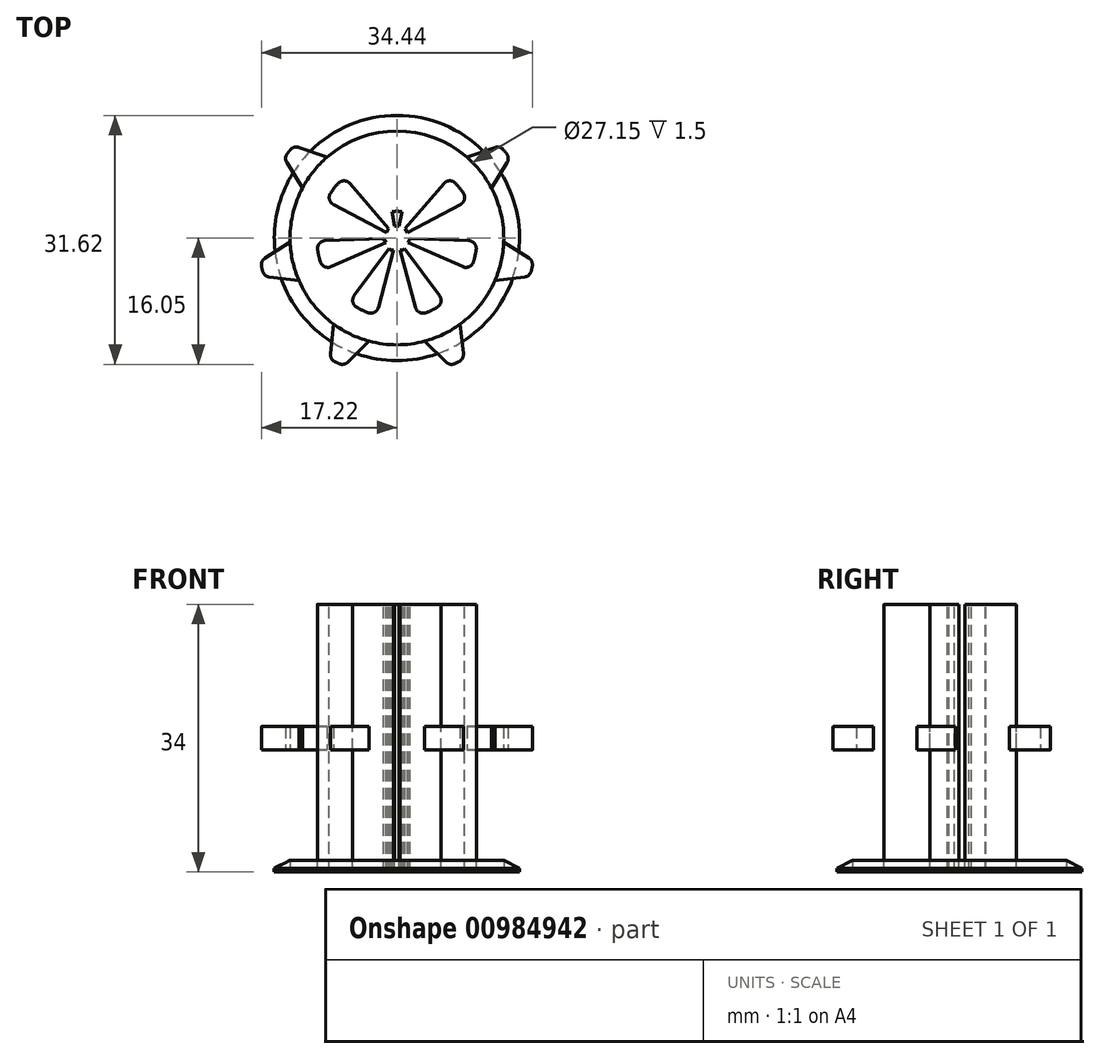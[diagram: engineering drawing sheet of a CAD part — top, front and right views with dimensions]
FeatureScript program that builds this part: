
annotation { "Feature Type Name" : "Feature", "Feature Type Description" : "" }
export const myFeature = defineFeature(function(context is Context, id is Id, definition is map)
    precondition{}
    {
        {
            var Q0;
            Q0=qCreatedBy(makeId("Top.planeOp"),FACE);
            var sketch = newSketch(context, id + "F0", { "sketchPlane" : qUnion([Q0])});
            skCircle(sketch, "E0", {"center": v(0, 0) * mm, "radius": 13.57 * mm});
            skSolve(sketch);
        }
        {
            var Q0;
            Q0=makeQuery(id+"F0.imprint","IMPRINT",FACE,{"disambiguationData":[TD([[makeQuery(id+"F0.imprint","IMPRINT",EDGE,{"derivedFrom":sQuery(id+"F0.wireOp",EDGE,"E0")}),1.0]])]});
            extrude(context, id + "F1", {"entities" : qUnion([Q0]), "endBound" : BoundingType.SYMMETRIC, "depth" : 34 * mm, "offsetDistance" : 25 * mm});
        }
        {
            var Q0;
            Q0=qCreatedBy(makeId("Top.planeOp"),FACE);
            var sketch = newSketch(context, id + "F2", { "sketchPlane" : qUnion([Q0])});
            skPoint(sketch, "E1", {"position": v(0, 17.57) * mm});
            skPoint(sketch, "E2", {"position": v(15.3, 12.2) * mm});
            skPoint(sketch, "E3", {"position": v(19.08, -4.36) * mm});
            skPoint(sketch, "E4", {"position": v(8.5, -17.64) * mm});
            skPoint(sketch, "E5", {"position": v(-8.5, -17.64) * mm});
            skPoint(sketch, "E6", {"position": v(-19.08, -4.36) * mm});
            skPoint(sketch, "E7", {"position": v(-15.3, 12.2) * mm});
            skArc(sketch, "E8", {"start": v(-1, 17.55) * mm, "mid": v(0, 17.57) * mm, "end": v(1, 17.55) * mm});
            skPoint(sketch, "E9", {"position": v(-12.18, 9.71) * mm});
            skPoint(sketch, "E10", {"position": v(12.18, 9.71) * mm});
            skPoint(sketch, "E11", {"position": v(15.18, -3.47) * mm});
            skPoint(sketch, "E12", {"position": v(6.76, -14.03) * mm});
            skPoint(sketch, "E13", {"position": v(-6.76, -14.03) * mm});
            skPoint(sketch, "E14", {"position": v(-15.18, -3.47) * mm});
            skPoint(sketch, "E15", {"position": v(0, 13.57) * mm});
            skArc(sketch, "E16", {"start": v(-2.5, 13.34) * mm, "mid": v(0, 13.57) * mm, "end": v(2.5, 13.34) * mm});
            skLineSegment(sketch, "E17", {"start": v(-2.5, 13.34) * mm, "end": v(-1, 17.55) * mm});
            skLineSegment(sketch, "E18", {"start": v(1, 17.55) * mm, "end": v(2.5, 13.34) * mm});
            skLineSegment(sketch, "E19.1.0", {"start": v(14.34, 10.16) * mm, "end": v(11.99, 6.36) * mm});
            skArc(sketch, "E19.1.1", {"start": v(8.87, 10.27) * mm, "mid": v(10.61, 8.46) * mm, "end": v(11.99, 6.36) * mm});
            skLineSegment(sketch, "E19.1.2", {"start": v(8.87, 10.27) * mm, "end": v(13.1, 11.72) * mm});
            skArc(sketch, "E19.1.3", {"start": v(13.1, 11.72) * mm, "mid": v(13.74, 10.96) * mm, "end": v(14.34, 10.16) * mm});
            skLineSegment(sketch, "E19.2.0", {"start": v(16.88, -4.88) * mm, "end": v(12.45, -5.4) * mm});
            skArc(sketch, "E19.2.1", {"start": v(13.56, -0.53) * mm, "mid": v(13.23, -3.02) * mm, "end": v(12.45, -5.4) * mm});
            skLineSegment(sketch, "E19.2.2", {"start": v(13.56, -0.53) * mm, "end": v(17.33, -2.93) * mm});
            skArc(sketch, "E19.2.3", {"start": v(17.33, -2.93) * mm, "mid": v(17.13, -3.91) * mm, "end": v(16.88, -4.88) * mm});
            skLineSegment(sketch, "E19.3.0", {"start": v(6.71, -16.24) * mm, "end": v(3.54, -13.1) * mm});
            skArc(sketch, "E19.3.1", {"start": v(8.04, -10.94) * mm, "mid": v(5.89, -12.23) * mm, "end": v(3.54, -13.1) * mm});
            skLineSegment(sketch, "E19.3.2", {"start": v(8.04, -10.94) * mm, "end": v(8.51, -15.37) * mm});
            skArc(sketch, "E19.3.3", {"start": v(8.51, -15.37) * mm, "mid": v(7.63, -15.83) * mm, "end": v(6.71, -16.24) * mm});
            skLineSegment(sketch, "E19.4.0", {"start": v(-8.51, -15.37) * mm, "end": v(-8.04, -10.94) * mm});
            skArc(sketch, "E19.4.1", {"start": v(-3.54, -13.1) * mm, "mid": v(-5.89, -12.23) * mm, "end": v(-8.04, -10.94) * mm});
            skLineSegment(sketch, "E19.4.2", {"start": v(-3.54, -13.1) * mm, "end": v(-6.71, -16.24) * mm});
            skArc(sketch, "E19.4.3", {"start": v(-6.71, -16.24) * mm, "mid": v(-7.63, -15.83) * mm, "end": v(-8.51, -15.37) * mm});
            skLineSegment(sketch, "E19.5.0", {"start": v(-17.33, -2.93) * mm, "end": v(-13.56, -0.53) * mm});
            skArc(sketch, "E19.5.1", {"start": v(-12.45, -5.4) * mm, "mid": v(-13.23, -3.02) * mm, "end": v(-13.56, -0.53) * mm});
            skLineSegment(sketch, "E19.5.2", {"start": v(-12.45, -5.4) * mm, "end": v(-16.88, -4.88) * mm});
            skArc(sketch, "E19.5.3", {"start": v(-16.88, -4.88) * mm, "mid": v(-17.13, -3.91) * mm, "end": v(-17.33, -2.93) * mm});
            skLineSegment(sketch, "E19.6.0", {"start": v(-13.1, 11.72) * mm, "end": v(-8.87, 10.27) * mm});
            skArc(sketch, "E19.6.1", {"start": v(-11.99, 6.36) * mm, "mid": v(-10.61, 8.46) * mm, "end": v(-8.87, 10.27) * mm});
            skLineSegment(sketch, "E19.6.2", {"start": v(-11.99, 6.36) * mm, "end": v(-14.34, 10.16) * mm});
            skArc(sketch, "E19.6.3", {"start": v(-14.34, 10.16) * mm, "mid": v(-13.74, 10.96) * mm, "end": v(-13.1, 11.72) * mm});
            skLineSegment(sketch, "E19.anchor1", {"start": v(0, 0) * mm, "end": v(2.5, 13.34) * mm, "construction": true});
            skLineSegment(sketch, "E19.anchor2", {"start": v(0, 0) * mm, "end": v(-8.87, 10.27) * mm, "construction": true});
            skSolve(sketch);
        }
        {
            var Q0;
            Q0=makeQuery(id+"F2.imprint","IMPRINT",FACE,{"disambiguationData":[TD([[makeQuery(id+"F2.imprint","IMPRINT",EDGE,{"derivedFrom":sQuery(id+"F2.wireOp",EDGE,"E19.6.0")}),-1.0]])]});
            var Q1;
            Q1=makeQuery(id+"F2.imprint","IMPRINT",FACE,{"disambiguationData":[TD([[makeQuery(id+"F2.imprint","IMPRINT",EDGE,{"derivedFrom":sQuery(id+"F2.wireOp",EDGE,"E8")}),-1.0]])]});
            var Q2;
            Q2=makeQuery(id+"F2.imprint","IMPRINT",FACE,{"disambiguationData":[TD([[makeQuery(id+"F2.imprint","IMPRINT",EDGE,{"derivedFrom":sQuery(id+"F2.wireOp",EDGE,"E19.1.0")}),-1.0]])]});
            var Q3;
            Q3=makeQuery(id+"F2.imprint","IMPRINT",FACE,{"disambiguationData":[TD([[makeQuery(id+"F2.imprint","IMPRINT",EDGE,{"derivedFrom":sQuery(id+"F2.wireOp",EDGE,"E19.2.0")}),-1.0]])]});
            var Q4;
            Q4=makeQuery(id+"F2.imprint","IMPRINT",FACE,{"disambiguationData":[TD([[makeQuery(id+"F2.imprint","IMPRINT",EDGE,{"derivedFrom":sQuery(id+"F2.wireOp",EDGE,"E19.3.0")}),-1.0]])]});
            var Q5;
            Q5=makeQuery(id+"F2.imprint","IMPRINT",FACE,{"disambiguationData":[TD([[makeQuery(id+"F2.imprint","IMPRINT",EDGE,{"derivedFrom":sQuery(id+"F2.wireOp",EDGE,"E19.4.0")}),-1.0]])]});
            var Q6;
            Q6=makeQuery(id+"F2.imprint","IMPRINT",FACE,{"disambiguationData":[TD([[makeQuery(id+"F2.imprint","IMPRINT",EDGE,{"derivedFrom":sQuery(id+"F2.wireOp",EDGE,"E19.5.0")}),-1.0]])]});
            extrude(context, id + "F3", {"entities" : qUnion([Q0, Q1, Q2, Q3, Q4, Q5, Q6]), "operationType" : NewBodyOperationType.ADD, "endBound" : BoundingType.SYMMETRIC, "depth" : 3 * mm, "offsetDistance" : 25 * mm});
        }
        {
            var Q0;
            Q0=makeQuery(id+"F1.opExtrude","CAP_FACE",FACE,{"disambiguationData":[OSD([sQuery(id+"F0.wireOp",EDGE,"E0")])],"isStart":false});
            var sketch = newSketch(context, id + "F4", { "sketchPlane" : qUnion([Q0])});
            skLineSegment(sketch, "E20", {"start": v(0, 0) * mm, "end": v(0, 3.4) * mm});
            skLineSegment(sketch, "E21", {"start": v(0, 3.4) * mm, "end": v(0, 6.79) * mm});
            skLineSegment(sketch, "E22", {"start": v(0, 6.79) * mm, "end": v(0, 10.18) * mm});
            skLineSegment(sketch, "E23", {"start": v(0, 10.18) * mm, "end": v(0, 13.57) * mm});
            skArc(sketch, "E24", {"start": v(-1.9, 10) * mm, "mid": v(0, 10.18) * mm, "end": v(1.9, 10) * mm});
            skPoint(sketch, "E25", {"position": v(0, 10.18) * mm});
            skArc(sketch, "E26", {"start": v(-0.63, 3.33) * mm, "mid": v(0, 3.4) * mm, "end": v(0.63, 3.33) * mm});
            skPoint(sketch, "E27", {"position": v(0, 3.4) * mm});
            skLineSegment(sketch, "E28", {"start": v(0, 0) * mm, "end": v(-1.9, 10) * mm});
            skLineSegment(sketch, "E29", {"start": v(1.9, 10) * mm, "end": v(0, 0) * mm});
            skArc(sketch, "E30.1.0", {"start": v(-9, 4.75) * mm, "mid": v(-7.96, 6.35) * mm, "end": v(-6.64, 7.72) * mm});
            skLineSegment(sketch, "E30.1.1", {"start": v(-6.64, 7.72) * mm, "end": v(0, 0) * mm});
            skArc(sketch, "E30.1.2", {"start": v(-3, 1.58) * mm, "mid": v(-2.65, 2.12) * mm, "end": v(-2.21, 2.57) * mm});
            skLineSegment(sketch, "E30.1.3", {"start": v(0, 0) * mm, "end": v(-9, 4.75) * mm});
            skArc(sketch, "E30.2.0", {"start": v(-9.33, -4.07) * mm, "mid": v(-9.93, -2.27) * mm, "end": v(-10.17, -0.38) * mm});
            skLineSegment(sketch, "E30.2.1", {"start": v(-10.17, -0.38) * mm, "end": v(0, 0) * mm});
            skArc(sketch, "E30.2.2", {"start": v(-3.1, -1.36) * mm, "mid": v(-3.3, -0.76) * mm, "end": v(-3.4, -0.13) * mm});
            skLineSegment(sketch, "E30.2.3", {"start": v(0, 0) * mm, "end": v(-9.33, -4.07) * mm});
            skArc(sketch, "E30.3.0", {"start": v(-2.63, -9.83) * mm, "mid": v(-4.42, -9.17) * mm, "end": v(-6.05, -8.19) * mm});
            skLineSegment(sketch, "E30.3.1", {"start": v(-6.05, -8.19) * mm, "end": v(0, 0) * mm});
            skArc(sketch, "E30.3.2", {"start": v(-0.88, -3.28) * mm, "mid": v(-1.47, -3.06) * mm, "end": v(-2.02, -2.73) * mm});
            skLineSegment(sketch, "E30.3.3", {"start": v(0, 0) * mm, "end": v(-2.63, -9.83) * mm});
            skArc(sketch, "E30.4.0", {"start": v(6.05, -8.19) * mm, "mid": v(4.42, -9.17) * mm, "end": v(2.63, -9.83) * mm});
            skLineSegment(sketch, "E30.4.1", {"start": v(2.63, -9.83) * mm, "end": v(0, 0) * mm});
            skArc(sketch, "E30.4.2", {"start": v(2.02, -2.73) * mm, "mid": v(1.47, -3.06) * mm, "end": v(0.88, -3.28) * mm});
            skLineSegment(sketch, "E30.4.3", {"start": v(0, 0) * mm, "end": v(6.05, -8.19) * mm});
            skArc(sketch, "E30.5.0", {"start": v(10.17, -0.38) * mm, "mid": v(9.93, -2.27) * mm, "end": v(9.33, -4.07) * mm});
            skLineSegment(sketch, "E30.5.1", {"start": v(9.33, -4.07) * mm, "end": v(0, 0) * mm});
            skArc(sketch, "E30.5.2", {"start": v(3.4, -0.13) * mm, "mid": v(3.3, -0.76) * mm, "end": v(3.1, -1.36) * mm});
            skLineSegment(sketch, "E30.5.3", {"start": v(0, 0) * mm, "end": v(10.17, -0.38) * mm});
            skArc(sketch, "E30.6.0", {"start": v(6.64, 7.72) * mm, "mid": v(7.96, 6.35) * mm, "end": v(9, 4.75) * mm});
            skLineSegment(sketch, "E30.6.1", {"start": v(9, 4.75) * mm, "end": v(0, 0) * mm});
            skArc(sketch, "E30.6.2", {"start": v(2.21, 2.57) * mm, "mid": v(2.65, 2.12) * mm, "end": v(3, 1.58) * mm});
            skLineSegment(sketch, "E30.6.3", {"start": v(0, 0) * mm, "end": v(6.64, 7.72) * mm});
            skCircle(sketch, "E31.cCircle", {"center": v(0, 0) * mm, "radius": 1.5 * mm, "construction": true});
            skLineSegment(sketch, "E31.0", {"start": v(-0.87, 1.5) * mm, "end": v(0.87, 1.5) * mm});
            skLineSegment(sketch, "E31.1", {"start": v(0.87, 1.5) * mm, "end": v(1.73, 0) * mm});
            skLineSegment(sketch, "E31.2", {"start": v(1.73, 0) * mm, "end": v(0.87, -1.5) * mm});
            skLineSegment(sketch, "E31.3", {"start": v(0.87, -1.5) * mm, "end": v(-0.87, -1.5) * mm});
            skLineSegment(sketch, "E31.4", {"start": v(-0.87, -1.5) * mm, "end": v(-1.73, 0) * mm});
            skLineSegment(sketch, "E31.5", {"start": v(-1.73, 0) * mm, "end": v(-0.87, 1.5) * mm});
            skPoint(sketch, "E31.0.midPoint", {"position": v(0, 1.5) * mm});
            skSolve(sketch);
        }
        {
            var Q0;
            {var subQ0=sQuery(id+"F4.wireOp",EDGE,"E30.1.0");Q0=makeQuery(id+"F4.imprint","IMPRINT",FACE,{"disambiguationData":[TD([[makeQuery(id+"F4.imprint","IMPRINT",EDGE,{"derivedFrom":subQ0}),-1.0]])]});}
            var Q1;
            {var subQ1=sQuery(id+"F4.wireOp",EDGE,"E21");Q1=makeQuery(id+"F4.imprint","IMPRINT",FACE,{"disambiguationData":[TD([[makeQuery(id+"F4.imprint","IMPRINT",EDGE,{"derivedFrom":subQ1}),1.0]])]});}
            var Q2;
            {var subQ5=sQuery(id+"F4.wireOp",EDGE,"E21");Q2=makeQuery(id+"F4.imprint","IMPRINT",FACE,{"disambiguationData":[TD([[makeQuery(id+"F4.imprint","IMPRINT",EDGE,{"derivedFrom":subQ5}),-1.0]])]});}
            var Q3;
            {var subQ0=sQuery(id+"F4.wireOp",EDGE,"E30.6.0");Q3=makeQuery(id+"F4.imprint","IMPRINT",FACE,{"disambiguationData":[TD([[makeQuery(id+"F4.imprint","IMPRINT",EDGE,{"derivedFrom":subQ0}),-1.0]])]});}
            var Q4;
            {var subQ0=sQuery(id+"F4.wireOp",EDGE,"E30.5.0");Q4=makeQuery(id+"F4.imprint","IMPRINT",FACE,{"disambiguationData":[TD([[makeQuery(id+"F4.imprint","IMPRINT",EDGE,{"derivedFrom":subQ0}),-1.0]])]});}
            var Q5;
            {var subQ0=sQuery(id+"F4.wireOp",EDGE,"E30.4.0");Q5=makeQuery(id+"F4.imprint","IMPRINT",FACE,{"disambiguationData":[TD([[makeQuery(id+"F4.imprint","IMPRINT",EDGE,{"derivedFrom":subQ0}),-1.0]])]});}
            var Q6;
            {var subQ0=sQuery(id+"F4.wireOp",EDGE,"E30.3.0");Q6=makeQuery(id+"F4.imprint","IMPRINT",FACE,{"disambiguationData":[TD([[makeQuery(id+"F4.imprint","IMPRINT",EDGE,{"derivedFrom":subQ0}),-1.0]])]});}
            var Q7;
            {var subQ0=sQuery(id+"F4.wireOp",EDGE,"E30.2.0");Q7=makeQuery(id+"F4.imprint","IMPRINT",FACE,{"disambiguationData":[TD([[makeQuery(id+"F4.imprint","IMPRINT",EDGE,{"derivedFrom":subQ0}),-1.0]])]});}
            var Q8;
            {var subQ3=sQuery(id+"F4.wireOp",EDGE,"83845be1-feb7-4ae9-bd42-3e984bab1aa7.5");var subQ5=sQuery(id+"F4.wireOp",EDGE,"83845be1-feb7-4ae9-bd42-3e984bab1aa7.4");var subQ7=makeQuery(id+"F4.imprint","INTERSECT",VERTEX,{"derivedFrom":[subQ5,subQ3]});Q8=makeQuery(id+"F4.imprint","IMPRINT",FACE,{"disambiguationData":[TD([[makeQuery(id+"F4.imprint","IMPRINT",EDGE,{"disambiguationData":[TD([[subQ7,1.0]])],"derivedFrom":subQ5}),-1.0]])]});}
            var Q9;
            {var subQ1=sQuery(id+"F4.wireOp",EDGE,"E28");var subQ3=sQuery(id+"F4.wireOp",EDGE,"83845be1-feb7-4ae9-bd42-3e984bab1aa7.5");var subQ4=makeQuery(id+"F4.imprint","INTERSECT",VERTEX,{"derivedFrom":[subQ1,subQ3]});Q9=makeQuery(id+"F4.imprint","IMPRINT",FACE,{"disambiguationData":[TD([[makeQuery(id+"F4.imprint","IMPRINT",EDGE,{"disambiguationData":[TD([[subQ4,1.0]])],"derivedFrom":subQ3}),-1.0]])]});}
            var Q10;
            {var subQ0=sQuery(id+"F4.wireOp",EDGE,"E28");var subQ3=sQuery(id+"F4.wireOp",EDGE,"83845be1-feb7-4ae9-bd42-3e984bab1aa7.5");var subQ5=makeQuery(id+"F4.imprint","INTERSECT",VERTEX,{"derivedFrom":[subQ0,subQ3]});Q10=makeQuery(id+"F4.imprint","IMPRINT",FACE,{"disambiguationData":[TD([[makeQuery(id+"F4.imprint","IMPRINT",EDGE,{"disambiguationData":[TD([[subQ5,-1.0]])],"derivedFrom":subQ3}),-1.0]])]});}
            var Q11;
            {var subQ0=sQuery(id+"F4.wireOp",EDGE,"E29");var subQ3=sQuery(id+"F4.wireOp",EDGE,"83845be1-feb7-4ae9-bd42-3e984bab1aa7.0");var subQ5=makeQuery(id+"F4.imprint","INTERSECT",VERTEX,{"derivedFrom":[subQ0,subQ3]});Q11=makeQuery(id+"F4.imprint","IMPRINT",FACE,{"disambiguationData":[TD([[makeQuery(id+"F4.imprint","IMPRINT",EDGE,{"disambiguationData":[TD([[subQ5,1.0]])],"derivedFrom":subQ3}),-1.0]])]});}
            var Q12;
            {var subQ1=sQuery(id+"F4.wireOp",EDGE,"E29");var subQ3=sQuery(id+"F4.wireOp",EDGE,"83845be1-feb7-4ae9-bd42-3e984bab1aa7.0");var subQ4=makeQuery(id+"F4.imprint","INTERSECT",VERTEX,{"derivedFrom":[subQ1,subQ3]});Q12=makeQuery(id+"F4.imprint","IMPRINT",FACE,{"disambiguationData":[TD([[makeQuery(id+"F4.imprint","IMPRINT",EDGE,{"disambiguationData":[TD([[subQ4,-1.0]])],"derivedFrom":subQ3}),-1.0]])]});}
            var Q13;
            {var subQ3=sQuery(id+"F4.wireOp",EDGE,"83845be1-feb7-4ae9-bd42-3e984bab1aa7.1");var subQ5=sQuery(id+"F4.wireOp",EDGE,"83845be1-feb7-4ae9-bd42-3e984bab1aa7.0");var subQ7=makeQuery(id+"F4.imprint","INTERSECT",VERTEX,{"derivedFrom":[subQ5,subQ3]});Q13=makeQuery(id+"F4.imprint","IMPRINT",FACE,{"disambiguationData":[TD([[makeQuery(id+"F4.imprint","IMPRINT",EDGE,{"disambiguationData":[TD([[subQ7,1.0]])],"derivedFrom":subQ5}),-1.0]])]});}
            var Q14;
            {var subQ1=sQuery(id+"F4.wireOp",EDGE,"E30.5.3");var subQ3=sQuery(id+"F4.wireOp",EDGE,"83845be1-feb7-4ae9-bd42-3e984bab1aa7.1");var subQ4=makeQuery(id+"F4.imprint","INTERSECT",VERTEX,{"derivedFrom":[subQ1,subQ3]});Q14=makeQuery(id+"F4.imprint","IMPRINT",FACE,{"disambiguationData":[TD([[makeQuery(id+"F4.imprint","IMPRINT",EDGE,{"disambiguationData":[TD([[subQ4,1.0]])],"derivedFrom":subQ3}),-1.0]])]});}
            var Q15;
            {var subQ1=sQuery(id+"F4.wireOp",EDGE,"E30.5.1");var subQ3=sQuery(id+"F4.wireOp",EDGE,"83845be1-feb7-4ae9-bd42-3e984bab1aa7.1");var subQ4=makeQuery(id+"F4.imprint","INTERSECT",VERTEX,{"derivedFrom":[subQ1,subQ3]});Q15=makeQuery(id+"F4.imprint","IMPRINT",FACE,{"disambiguationData":[TD([[makeQuery(id+"F4.imprint","IMPRINT",EDGE,{"disambiguationData":[TD([[subQ4,1.0]])],"derivedFrom":subQ3}),-1.0]])]});}
            var Q16;
            {var subQ3=sQuery(id+"F4.wireOp",EDGE,"83845be1-feb7-4ae9-bd42-3e984bab1aa7.2");var subQ5=sQuery(id+"F4.wireOp",EDGE,"83845be1-feb7-4ae9-bd42-3e984bab1aa7.1");var subQ6=makeQuery(id+"F4.imprint","INTERSECT",VERTEX,{"derivedFrom":[subQ5,subQ3]});Q16=makeQuery(id+"F4.imprint","IMPRINT",FACE,{"disambiguationData":[TD([[makeQuery(id+"F4.imprint","IMPRINT",EDGE,{"disambiguationData":[TD([[subQ6,1.0]])],"derivedFrom":subQ5}),-1.0]])]});}
            var Q17;
            {var subQ1=sQuery(id+"F4.wireOp",EDGE,"E30.4.1");var subQ3=sQuery(id+"F4.wireOp",EDGE,"83845be1-feb7-4ae9-bd42-3e984bab1aa7.2");var subQ4=makeQuery(id+"F4.imprint","INTERSECT",VERTEX,{"derivedFrom":[subQ1,subQ3]});Q17=makeQuery(id+"F4.imprint","IMPRINT",FACE,{"disambiguationData":[TD([[makeQuery(id+"F4.imprint","IMPRINT",EDGE,{"disambiguationData":[TD([[subQ4,1.0]])],"derivedFrom":subQ3}),-1.0]])]});}
            var Q18;
            {var subQ3=sQuery(id+"F4.wireOp",EDGE,"83845be1-feb7-4ae9-bd42-3e984bab1aa7.3");var subQ5=sQuery(id+"F4.wireOp",EDGE,"83845be1-feb7-4ae9-bd42-3e984bab1aa7.2");var subQ7=makeQuery(id+"F4.imprint","INTERSECT",VERTEX,{"derivedFrom":[subQ5,subQ3]});Q18=makeQuery(id+"F4.imprint","IMPRINT",FACE,{"disambiguationData":[TD([[makeQuery(id+"F4.imprint","IMPRINT",EDGE,{"disambiguationData":[TD([[subQ7,1.0]])],"derivedFrom":subQ5}),-1.0]])]});}
            var Q19;
            {var subQ1=sQuery(id+"F4.wireOp",EDGE,"E30.3.1");var subQ3=sQuery(id+"F4.wireOp",EDGE,"83845be1-feb7-4ae9-bd42-3e984bab1aa7.3");var subQ4=makeQuery(id+"F4.imprint","INTERSECT",VERTEX,{"derivedFrom":[subQ1,subQ3]});Q19=makeQuery(id+"F4.imprint","IMPRINT",FACE,{"disambiguationData":[TD([[makeQuery(id+"F4.imprint","IMPRINT",EDGE,{"disambiguationData":[TD([[subQ4,1.0]])],"derivedFrom":subQ3}),-1.0]])]});}
            var Q20;
            {var subQ3=sQuery(id+"F4.wireOp",EDGE,"83845be1-feb7-4ae9-bd42-3e984bab1aa7.4");var subQ5=sQuery(id+"F4.wireOp",EDGE,"83845be1-feb7-4ae9-bd42-3e984bab1aa7.3");var subQ7=makeQuery(id+"F4.imprint","INTERSECT",VERTEX,{"derivedFrom":[subQ5,subQ3]});Q20=makeQuery(id+"F4.imprint","IMPRINT",FACE,{"disambiguationData":[TD([[makeQuery(id+"F4.imprint","IMPRINT",EDGE,{"disambiguationData":[TD([[subQ7,1.0]])],"derivedFrom":subQ5}),-1.0]])]});}
            var Q21;
            {var subQ1=sQuery(id+"F4.wireOp",EDGE,"E30.2.1");var subQ3=sQuery(id+"F4.wireOp",EDGE,"83845be1-feb7-4ae9-bd42-3e984bab1aa7.4");var subQ4=makeQuery(id+"F4.imprint","INTERSECT",VERTEX,{"derivedFrom":[subQ1,subQ3]});Q21=makeQuery(id+"F4.imprint","IMPRINT",FACE,{"disambiguationData":[TD([[makeQuery(id+"F4.imprint","IMPRINT",EDGE,{"disambiguationData":[TD([[subQ4,1.0]])],"derivedFrom":subQ3}),-1.0]])]});}
            var Q22;
            {var subQ1=sQuery(id+"F4.wireOp",EDGE,"E30.1.3");var subQ3=sQuery(id+"F4.wireOp",EDGE,"83845be1-feb7-4ae9-bd42-3e984bab1aa7.4");var subQ4=makeQuery(id+"F4.imprint","INTERSECT",VERTEX,{"derivedFrom":[subQ1,subQ3]});Q22=makeQuery(id+"F4.imprint","IMPRINT",FACE,{"disambiguationData":[TD([[makeQuery(id+"F4.imprint","IMPRINT",EDGE,{"disambiguationData":[TD([[subQ4,1.0]])],"derivedFrom":subQ3}),-1.0]])]});}
            var Q23;
            {var subQ3=sQuery(id+"F4.wireOp",EDGE,"E31.2");var subQ5=sQuery(id+"F4.wireOp",EDGE,"E31.1");var subQ7=makeQuery(id+"F4.imprint","INTERSECT",VERTEX,{"derivedFrom":[subQ5,subQ3]});Q23=makeQuery(id+"F4.imprint","IMPRINT",FACE,{"disambiguationData":[TD([[makeQuery(id+"F4.imprint","IMPRINT",EDGE,{"disambiguationData":[TD([[subQ7,1.0]])],"derivedFrom":subQ5}),-1.0]])]});}
            var Q24;
            {var subQ1=sQuery(id+"F4.wireOp",EDGE,"E30.5.1");var subQ3=sQuery(id+"F4.wireOp",EDGE,"E31.2");var subQ4=makeQuery(id+"F4.imprint","INTERSECT",VERTEX,{"derivedFrom":[subQ1,subQ3]});Q24=makeQuery(id+"F4.imprint","IMPRINT",FACE,{"disambiguationData":[TD([[makeQuery(id+"F4.imprint","IMPRINT",EDGE,{"disambiguationData":[TD([[subQ4,1.0]])],"derivedFrom":subQ3}),-1.0]])]});}
            var Q25;
            {var subQ1=sQuery(id+"F4.wireOp",EDGE,"E30.4.3");var subQ3=sQuery(id+"F4.wireOp",EDGE,"E31.2");var subQ4=makeQuery(id+"F4.imprint","INTERSECT",VERTEX,{"derivedFrom":[subQ1,subQ3]});Q25=makeQuery(id+"F4.imprint","IMPRINT",FACE,{"disambiguationData":[TD([[makeQuery(id+"F4.imprint","IMPRINT",EDGE,{"disambiguationData":[TD([[subQ4,1.0]])],"derivedFrom":subQ3}),-1.0]])]});}
            var Q26;
            {var subQ3=sQuery(id+"F4.wireOp",EDGE,"E31.3");var subQ5=sQuery(id+"F4.wireOp",EDGE,"E31.2");var subQ7=makeQuery(id+"F4.imprint","INTERSECT",VERTEX,{"derivedFrom":[subQ5,subQ3]});Q26=makeQuery(id+"F4.imprint","IMPRINT",FACE,{"disambiguationData":[TD([[makeQuery(id+"F4.imprint","IMPRINT",EDGE,{"disambiguationData":[TD([[subQ7,1.0]])],"derivedFrom":subQ5}),-1.0]])]});}
            var Q27;
            {var subQ1=sQuery(id+"F4.wireOp",EDGE,"E30.3.3");var subQ3=sQuery(id+"F4.wireOp",EDGE,"E31.3");var subQ4=makeQuery(id+"F4.imprint","INTERSECT",VERTEX,{"derivedFrom":[subQ1,subQ3]});Q27=makeQuery(id+"F4.imprint","IMPRINT",FACE,{"disambiguationData":[TD([[makeQuery(id+"F4.imprint","IMPRINT",EDGE,{"disambiguationData":[TD([[subQ4,1.0]])],"derivedFrom":subQ3}),-1.0]])]});}
            var Q28;
            {var subQ3=sQuery(id+"F4.wireOp",EDGE,"E31.4");var subQ5=sQuery(id+"F4.wireOp",EDGE,"E31.3");var subQ7=makeQuery(id+"F4.imprint","INTERSECT",VERTEX,{"derivedFrom":[subQ5,subQ3]});Q28=makeQuery(id+"F4.imprint","IMPRINT",FACE,{"disambiguationData":[TD([[makeQuery(id+"F4.imprint","IMPRINT",EDGE,{"disambiguationData":[TD([[subQ7,1.0]])],"derivedFrom":subQ5}),-1.0]])]});}
            var Q29;
            {var subQ1=sQuery(id+"F4.wireOp",EDGE,"E30.2.3");var subQ3=sQuery(id+"F4.wireOp",EDGE,"E31.4");var subQ4=makeQuery(id+"F4.imprint","INTERSECT",VERTEX,{"derivedFrom":[subQ1,subQ3]});Q29=makeQuery(id+"F4.imprint","IMPRINT",FACE,{"disambiguationData":[TD([[makeQuery(id+"F4.imprint","IMPRINT",EDGE,{"disambiguationData":[TD([[subQ4,1.0]])],"derivedFrom":subQ3}),-1.0]])]});}
            var Q30;
            {var subQ1=sQuery(id+"F4.wireOp",EDGE,"E30.2.1");var subQ3=sQuery(id+"F4.wireOp",EDGE,"E31.4");var subQ4=makeQuery(id+"F4.imprint","INTERSECT",VERTEX,{"derivedFrom":[subQ1,subQ3]});Q30=makeQuery(id+"F4.imprint","IMPRINT",FACE,{"disambiguationData":[TD([[makeQuery(id+"F4.imprint","IMPRINT",EDGE,{"disambiguationData":[TD([[subQ4,1.0]])],"derivedFrom":subQ3}),-1.0]])]});}
            var Q31;
            {var subQ3=sQuery(id+"F4.wireOp",EDGE,"E31.5");var subQ5=sQuery(id+"F4.wireOp",EDGE,"E31.4");var subQ6=makeQuery(id+"F4.imprint","INTERSECT",VERTEX,{"derivedFrom":[subQ5,subQ3]});Q31=makeQuery(id+"F4.imprint","IMPRINT",FACE,{"disambiguationData":[TD([[makeQuery(id+"F4.imprint","IMPRINT",EDGE,{"disambiguationData":[TD([[subQ6,1.0]])],"derivedFrom":subQ5}),-1.0]])]});}
            var Q32;
            {var subQ1=sQuery(id+"F4.wireOp",EDGE,"E30.1.1");var subQ3=sQuery(id+"F4.wireOp",EDGE,"E31.5");var subQ4=makeQuery(id+"F4.imprint","INTERSECT",VERTEX,{"derivedFrom":[subQ1,subQ3]});Q32=makeQuery(id+"F4.imprint","IMPRINT",FACE,{"disambiguationData":[TD([[makeQuery(id+"F4.imprint","IMPRINT",EDGE,{"disambiguationData":[TD([[subQ4,1.0]])],"derivedFrom":subQ3}),-1.0]])]});}
            var Q33;
            {var subQ3=sQuery(id+"F4.wireOp",EDGE,"E31.0");var subQ5=sQuery(id+"F4.wireOp",EDGE,"E31.5");var subQ7=makeQuery(id+"F4.imprint","INTERSECT",VERTEX,{"derivedFrom":[subQ3,subQ5]});Q33=makeQuery(id+"F4.imprint","IMPRINT",FACE,{"disambiguationData":[TD([[makeQuery(id+"F4.imprint","IMPRINT",EDGE,{"disambiguationData":[TD([[subQ7,-1.0]])],"derivedFrom":subQ3}),-1.0]])]});}
            var Q34;
            {var subQ1=sQuery(id+"F4.wireOp",EDGE,"E20");var subQ3=sQuery(id+"F4.wireOp",EDGE,"E31.0");var subQ4=makeQuery(id+"F4.imprint","INTERSECT",VERTEX,{"derivedFrom":[subQ1,subQ3]});Q34=makeQuery(id+"F4.imprint","IMPRINT",FACE,{"disambiguationData":[TD([[makeQuery(id+"F4.imprint","IMPRINT",EDGE,{"disambiguationData":[TD([[subQ4,1.0]])],"derivedFrom":subQ3}),-1.0]])]});}
            var Q35;
            {var subQ1=sQuery(id+"F4.wireOp",EDGE,"E20");var subQ3=sQuery(id+"F4.wireOp",EDGE,"E31.0");var subQ4=makeQuery(id+"F4.imprint","INTERSECT",VERTEX,{"derivedFrom":[subQ1,subQ3]});Q35=makeQuery(id+"F4.imprint","IMPRINT",FACE,{"disambiguationData":[TD([[makeQuery(id+"F4.imprint","IMPRINT",EDGE,{"disambiguationData":[TD([[subQ4,-1.0]])],"derivedFrom":subQ3}),-1.0]])]});}
            var Q36;
            {var subQ3=sQuery(id+"F4.wireOp",EDGE,"E31.0");var subQ5=sQuery(id+"F4.wireOp",EDGE,"E31.1");var subQ7=makeQuery(id+"F4.imprint","INTERSECT",VERTEX,{"derivedFrom":[subQ3,subQ5]});Q36=makeQuery(id+"F4.imprint","IMPRINT",FACE,{"disambiguationData":[TD([[makeQuery(id+"F4.imprint","IMPRINT",EDGE,{"disambiguationData":[TD([[subQ7,1.0]])],"derivedFrom":subQ3}),-1.0]])]});}
            var Q37;
            {var subQ1=sQuery(id+"F4.wireOp",EDGE,"E30.6.1");var subQ3=sQuery(id+"F4.wireOp",EDGE,"E31.1");var subQ4=makeQuery(id+"F4.imprint","INTERSECT",VERTEX,{"derivedFrom":[subQ1,subQ3]});Q37=makeQuery(id+"F4.imprint","IMPRINT",FACE,{"disambiguationData":[TD([[makeQuery(id+"F4.imprint","IMPRINT",EDGE,{"disambiguationData":[TD([[subQ4,1.0]])],"derivedFrom":subQ3}),-1.0]])]});}
            extrude(context, id + "F5", {"entities" : qUnion([Q0, Q1, Q2, Q3, Q4, Q5, Q6, Q7, Q8, Q9, Q10, Q11, Q12, Q13, Q14, Q15, Q16, Q17, Q18, Q19, Q20, Q21, Q22, Q23, Q24, Q25, Q26, Q27, Q28, Q29, Q30, Q31, Q32, Q33, Q34, Q35, Q36, Q37]), "operationType" : NewBodyOperationType.REMOVE, "oppositeDirection" : true, "depth" : 34 * mm, "offsetDistance" : 25 * mm});
        }
        {
            var Q0;
            Q0=makeQuery(id+"F5.boolean.opBoolean","COPY",EDGE,{"derivedFrom":makeQuery(id+"F5.opExtrude","SWEPT_EDGE",EDGE,{"disambiguationData":[OSD([sQuery(id+"F4.wireOp",EDGE,"E30.3.0"),sQuery(id+"F4.wireOp",EDGE,"E30.3.1")])]})});
            var Q1;
            Q1=makeQuery(id+"F5.boolean.opBoolean","COPY",EDGE,{"derivedFrom":makeQuery(id+"F5.opExtrude","SWEPT_EDGE",EDGE,{"disambiguationData":[OSD([sQuery(id+"F4.wireOp",EDGE,"E30.3.0"),sQuery(id+"F4.wireOp",EDGE,"E30.3.3")])]})});
            var Q2;
            Q2=makeQuery(id+"F5.boolean.opBoolean","COPY",EDGE,{"derivedFrom":makeQuery(id+"F5.opExtrude","SWEPT_EDGE",EDGE,{"disambiguationData":[OSD([sQuery(id+"F4.wireOp",EDGE,"E30.4.0"),sQuery(id+"F4.wireOp",EDGE,"E30.4.1")])]})});
            var Q3;
            Q3=makeQuery(id+"F5.boolean.opBoolean","COPY",EDGE,{"derivedFrom":makeQuery(id+"F5.opExtrude","SWEPT_EDGE",EDGE,{"disambiguationData":[OSD([sQuery(id+"F4.wireOp",EDGE,"E30.4.0"),sQuery(id+"F4.wireOp",EDGE,"E30.4.3")])]})});
            var Q4;
            Q4=makeQuery(id+"F5.boolean.opBoolean","COPY",EDGE,{"derivedFrom":makeQuery(id+"F5.opExtrude","SWEPT_EDGE",EDGE,{"disambiguationData":[OSD([sQuery(id+"F4.wireOp",EDGE,"E30.5.0"),sQuery(id+"F4.wireOp",EDGE,"E30.5.1")])]})});
            var Q5;
            Q5=makeQuery(id+"F5.boolean.opBoolean","COPY",EDGE,{"derivedFrom":makeQuery(id+"F5.opExtrude","SWEPT_EDGE",EDGE,{"disambiguationData":[OSD([sQuery(id+"F4.wireOp",EDGE,"E30.2.0"),sQuery(id+"F4.wireOp",EDGE,"E30.2.3")])]})});
            var Q6;
            Q6=makeQuery(id+"F5.boolean.opBoolean","COPY",EDGE,{"derivedFrom":makeQuery(id+"F5.opExtrude","SWEPT_EDGE",EDGE,{"disambiguationData":[OSD([sQuery(id+"F4.wireOp",EDGE,"E30.2.0"),sQuery(id+"F4.wireOp",EDGE,"E30.2.1")])]})});
            var Q7;
            Q7=makeQuery(id+"F5.boolean.opBoolean","COPY",EDGE,{"derivedFrom":makeQuery(id+"F5.opExtrude","SWEPT_EDGE",EDGE,{"disambiguationData":[OSD([sQuery(id+"F4.wireOp",EDGE,"E30.1.0"),sQuery(id+"F4.wireOp",EDGE,"E30.1.3")])]})});
            var Q8;
            Q8=makeQuery(id+"F5.boolean.opBoolean","COPY",EDGE,{"derivedFrom":makeQuery(id+"F5.opExtrude","SWEPT_EDGE",EDGE,{"disambiguationData":[OSD([sQuery(id+"F4.wireOp",EDGE,"E30.1.0"),sQuery(id+"F4.wireOp",EDGE,"E30.1.1")])]})});
            var Q9;
            Q9=makeQuery(id+"F5.boolean.opBoolean","COPY",EDGE,{"derivedFrom":makeQuery(id+"F5.opExtrude","SWEPT_EDGE",EDGE,{"disambiguationData":[OSD([sQuery(id+"F4.wireOp",EDGE,"E30.6.0"),sQuery(id+"F4.wireOp",EDGE,"E30.6.3")])]})});
            var Q10;
            Q10=makeQuery(id+"F5.boolean.opBoolean","COPY",EDGE,{"derivedFrom":makeQuery(id+"F5.opExtrude","SWEPT_EDGE",EDGE,{"disambiguationData":[OSD([sQuery(id+"F4.wireOp",EDGE,"E24"),sQuery(id+"F4.wireOp",EDGE,"E28")])]})});
            var Q11;
            Q11=makeQuery(id+"F5.boolean.opBoolean","COPY",EDGE,{"derivedFrom":makeQuery(id+"F5.opExtrude","SWEPT_EDGE",EDGE,{"disambiguationData":[OSD([sQuery(id+"F4.wireOp",EDGE,"E24"),sQuery(id+"F4.wireOp",EDGE,"E29")])]})});
            var Q12;
            Q12=makeQuery(id+"F5.boolean.opBoolean","COPY",EDGE,{"derivedFrom":makeQuery(id+"F5.opExtrude","SWEPT_EDGE",EDGE,{"disambiguationData":[OSD([sQuery(id+"F4.wireOp",EDGE,"E30.6.0"),sQuery(id+"F4.wireOp",EDGE,"E30.6.1")])]})});
            var Q13;
            Q13=makeQuery(id+"F5.boolean.opBoolean","COPY",EDGE,{"derivedFrom":makeQuery(id+"F5.opExtrude","SWEPT_EDGE",EDGE,{"disambiguationData":[OSD([sQuery(id+"F4.wireOp",EDGE,"E30.5.0"),sQuery(id+"F4.wireOp",EDGE,"E30.5.3")])]})});
            fillet(context, id + "F6", {"entities" : qUnion([Q0, Q1, Q2, Q3, Q4, Q5, Q6, Q7, Q8, Q9, Q10, Q11, Q12, Q13]), "radius" : 1 * mm, "tangentPropagation" : true, "allowEdgeOverflow" : false});
        }
        {
            var Q0;
            Q0=makeQuery(id+"F1.opExtrude","CAP_FACE",FACE,{"disambiguationData":[OSD([sQuery(id+"F0.wireOp",EDGE,"E0")])],"isStart":true});
            var sketch = newSketch(context, id + "F7", { "sketchPlane" : qUnion([Q0])});
            skCircle(sketch, "E32", {"center": v(0, 0) * mm, "radius": 13.57 * mm});
            skCircle(sketch, "E33", {"center": v(0, 0) * mm, "radius": 15.57 * mm});
            skSolve(sketch);
        }
        {
            var Q0;
            Q0=qSketchRegion(id+"F7",true);
            extrude(context, id + "F8", {"entities" : qUnion([Q0]), "operationType" : NewBodyOperationType.ADD, "oppositeDirection" : true, "depth" : 1.5 * mm, "offsetDistance" : 25 * mm});
        }
        {
            var Q0;
            Q0=makeQuery(id+"F8.opExtrude","CAP_EDGE",EDGE,{"disambiguationData":[OSD([sQuery(id+"F7.wireOp",EDGE,"E33")])],"isStart":false});
            chamfer(context, id + "F9", {"entities" : qUnion([Q0]), "chamferType" : ChamferType.TWO_OFFSETS, "width1" : 2 * mm, "oppositeDirection" : true, "width2" : 1 * mm, "tangentPropagation" : true});
        }
        {
            var Q0;
            Q0=makeQuery(id+"F3.opExtrude","SWEPT_EDGE",EDGE,{"disambiguationData":[OSD([sQuery(id+"F2.wireOp",EDGE,"E19.1.0"),sQuery(id+"F2.wireOp",EDGE,"E19.1.3")])]});
            var Q1;
            Q1=makeQuery(id+"F3.opExtrude","SWEPT_EDGE",EDGE,{"disambiguationData":[OSD([sQuery(id+"F2.wireOp",EDGE,"E19.1.2"),sQuery(id+"F2.wireOp",EDGE,"E19.1.3")])]});
            var Q2;
            Q2=makeQuery(id+"F3.opExtrude","SWEPT_EDGE",EDGE,{"disambiguationData":[OSD([sQuery(id+"F2.wireOp",EDGE,"E8"),sQuery(id+"F2.wireOp",EDGE,"E18")])]});
            var Q3;
            Q3=makeQuery(id+"F3.opExtrude","SWEPT_EDGE",EDGE,{"disambiguationData":[OSD([sQuery(id+"F2.wireOp",EDGE,"E8"),sQuery(id+"F2.wireOp",EDGE,"E17")])]});
            var Q4;
            Q4=makeQuery(id+"F3.opExtrude","SWEPT_EDGE",EDGE,{"disambiguationData":[OSD([sQuery(id+"F2.wireOp",EDGE,"E19.6.0"),sQuery(id+"F2.wireOp",EDGE,"E19.6.3")])]});
            var Q5;
            Q5=makeQuery(id+"F3.opExtrude","SWEPT_EDGE",EDGE,{"disambiguationData":[OSD([sQuery(id+"F2.wireOp",EDGE,"E19.6.2"),sQuery(id+"F2.wireOp",EDGE,"E19.6.3")])]});
            var Q6;
            Q6=makeQuery(id+"F3.opExtrude","SWEPT_EDGE",EDGE,{"disambiguationData":[OSD([sQuery(id+"F2.wireOp",EDGE,"E19.5.0"),sQuery(id+"F2.wireOp",EDGE,"E19.5.3")])]});
            var Q7;
            Q7=makeQuery(id+"F3.opExtrude","SWEPT_EDGE",EDGE,{"disambiguationData":[OSD([sQuery(id+"F2.wireOp",EDGE,"E19.5.2"),sQuery(id+"F2.wireOp",EDGE,"E19.5.3")])]});
            var Q8;
            Q8=makeQuery(id+"F3.opExtrude","SWEPT_EDGE",EDGE,{"disambiguationData":[OSD([sQuery(id+"F2.wireOp",EDGE,"E19.4.0"),sQuery(id+"F2.wireOp",EDGE,"E19.4.3")])]});
            var Q9;
            Q9=makeQuery(id+"F3.opExtrude","SWEPT_EDGE",EDGE,{"disambiguationData":[OSD([sQuery(id+"F2.wireOp",EDGE,"E19.4.2"),sQuery(id+"F2.wireOp",EDGE,"E19.4.3")])]});
            var Q10;
            Q10=makeQuery(id+"F3.opExtrude","SWEPT_EDGE",EDGE,{"disambiguationData":[OSD([sQuery(id+"F2.wireOp",EDGE,"E19.3.0"),sQuery(id+"F2.wireOp",EDGE,"E19.3.3")])]});
            var Q11;
            Q11=makeQuery(id+"F3.opExtrude","SWEPT_EDGE",EDGE,{"disambiguationData":[OSD([sQuery(id+"F2.wireOp",EDGE,"E19.3.2"),sQuery(id+"F2.wireOp",EDGE,"E19.3.3")])]});
            var Q12;
            Q12=makeQuery(id+"F3.opExtrude","SWEPT_EDGE",EDGE,{"disambiguationData":[OSD([sQuery(id+"F2.wireOp",EDGE,"E19.2.0"),sQuery(id+"F2.wireOp",EDGE,"E19.2.3")])]});
            var Q13;
            Q13=makeQuery(id+"F3.opExtrude","SWEPT_EDGE",EDGE,{"disambiguationData":[OSD([sQuery(id+"F2.wireOp",EDGE,"E19.2.2"),sQuery(id+"F2.wireOp",EDGE,"E19.2.3")])]});
            fillet(context, id + "F10", {"entities" : qUnion([Q0, Q1, Q2, Q3, Q4, Q5, Q6, Q7, Q8, Q9, Q10, Q11, Q12, Q13]), "radius" : 1 * mm, "tangentPropagation" : true, "allowEdgeOverflow" : false});
        }
    });
